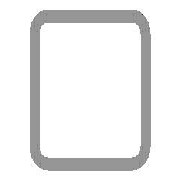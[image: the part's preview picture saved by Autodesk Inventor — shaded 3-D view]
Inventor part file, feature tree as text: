
AUTODESK INVENTOR PART (.ipt)
format: ipt  version: 2025 (Build 290162010, 162A)  size: 131,584 bytes
history: native  units: mm (DEFAULTED — no unit token found)
features: other x4, sketch x1, plane x1
ambient origin geometry x8: Origin, YZ Plane, XZ Plane, XY Plane, X Axis, Y Axis, Z Axis, Center Point
bodies: Solid1 (feature_tree), Body (feature_tree)
feature tree (6):
  parser-record x1  (decoder bookkeeping rows leaked as tree rows — omitted from the tree; the rows remain in map.json)
  other  "Driven Length"
  other  "Start Plane"
  other  "End Plane"
  sketch  "Sketch3"  dims[d3=2100.0mm d4=0.0mm d7=4.0mm d9=40.0mm d11=40.0mm d12=2.0mm d13=-0.0mm d14=2100.0mm d15=20.0mm d16=20.0mm d17=90.0deg d18=2100.0mm]
  plane  "Work Plane3"
